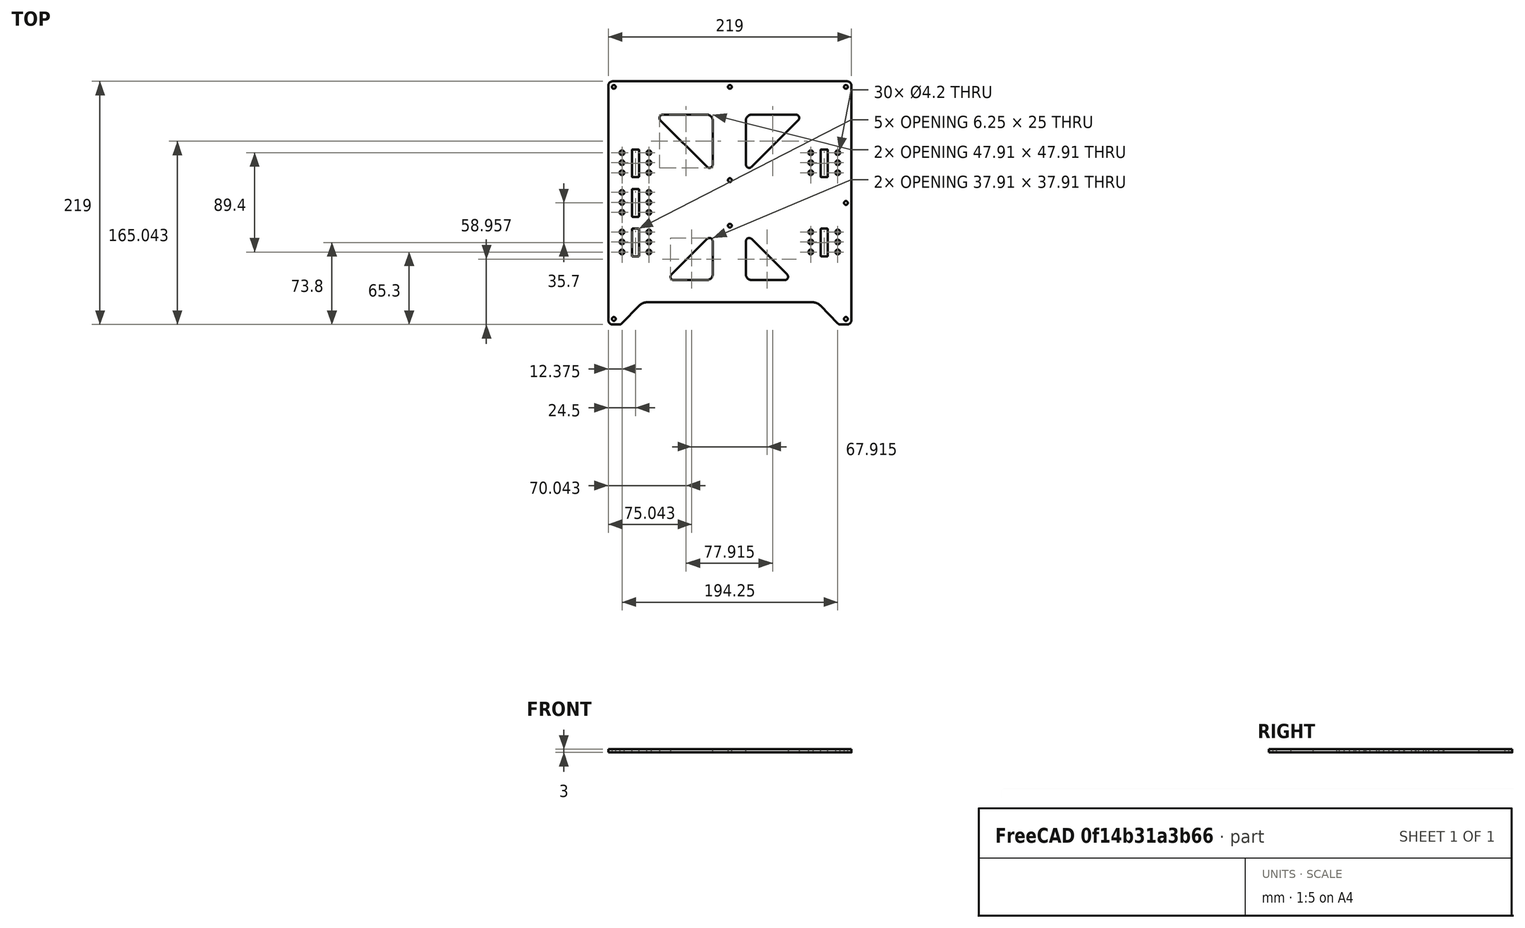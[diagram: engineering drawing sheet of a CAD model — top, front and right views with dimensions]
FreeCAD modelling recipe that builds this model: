
FCSTD DOCUMENT  (FreeCAD 0.18R)
Label: carriage-plate
License: All rights reserved
LicenseURL: http://en.wikipedia.org/wiki/All_rights_reserved
objects: Sketcher::SketchObject×1, PartDesign::Pad×1, PartDesign::Body×1
note: 4 computed .brp shape members not serialized (recipe doc carries the construction recipe); baked Part::Feature solids carry a one-line shape summary decoded from their .brp

FEATURE [Sketcher::SketchObject] Sketch009  label="Plate Sketch"
  MapMode = 5
  Support = -> [XY_Plane]
  sketch-geometry (118):
    g0: LineSegment StartX=-215 StartY=219 StartZ=0 EndX=-4 EndY=219 EndZ=0
    g1: LineSegment StartX=0 StartY=215 StartZ=0 EndX=0 EndY=4 EndZ=0
    g2: ArcOfCircle CenterX=-4 CenterY=215 CenterZ=0 NormalX=0 NormalY=0 NormalZ=1 AngleXU=0 Radius=4 StartAngle=-3.6e-15 EndAngle=1.5708
    g3: LineSegment StartX=-219 StartY=215 StartZ=0 EndX=-219 EndY=4 EndZ=0
    g4: ArcOfCircle CenterX=-215 CenterY=215 CenterZ=0 NormalX=0 NormalY=0 NormalZ=1 AngleXU=0 Radius=4 StartAngle=1.5708 EndAngle=3.14159
    g5: LineSegment StartX=-10 StartY=0 StartZ=0 EndX=-4 EndY=0 EndZ=0
    g6: ArcOfCircle CenterX=-4 CenterY=4 CenterZ=0 NormalX=0 NormalY=0 NormalZ=1 AngleXU=0 Radius=4 StartAngle=4.71239 EndAngle=6.28319
    g7: LineSegment StartX=-215 StartY=1.3e-15 StartZ=0 EndX=-209 EndY=1.3e-15 EndZ=0
    g8: ArcOfCircle CenterX=-215 CenterY=4 CenterZ=0 NormalX=0 NormalY=0 NormalZ=1 AngleXU=0 Radius=4 StartAngle=3.14159 EndAngle=4.71239
    g9: LineSegment StartX=-184 StartY=20 StartZ=0 EndX=-35 EndY=20 EndZ=0
    g10: LineSegment StartX=-27.817 StartY=16.9574 StartZ=0 EndX=-12.3608 EndY=1 EndZ=0
    g11: ArcOfCircle CenterX=-10 CenterY=3.28664 CenterZ=0 NormalX=0 NormalY=0 NormalZ=1 AngleXU=0 Radius=3.28664 StartAngle=3.91104 EndAngle=4.71239
    g12: ArcOfCircle CenterX=-35 CenterY=10 CenterZ=0 NormalX=0 NormalY=0 NormalZ=1 AngleXU=0 Radius=10 StartAngle=0.769447 EndAngle=1.5708
    g13: LineSegment StartX=-206.639 StartY=1 StartZ=0 EndX=-191.183 EndY=16.9574 EndZ=0
    g14: ArcOfCircle CenterX=-184 CenterY=10 CenterZ=0 NormalX=0 NormalY=0 NormalZ=1 AngleXU=0 Radius=10 StartAngle=1.5708 EndAngle=2.37215
    g15: ArcOfCircle CenterX=-209 CenterY=3.28664 CenterZ=0 NormalX=0 NormalY=0 NormalZ=1 AngleXU=0 Radius=3.28664 StartAngle=4.71239 EndAngle=5.51374
    g16: Circle CenterX=-5 CenterY=214 CenterZ=0 NormalX=0 NormalY=0 NormalZ=1 AngleXU=0 Radius=1.7
    g17: Circle CenterX=-5 CenterY=109.5 CenterZ=0 NormalX=0 NormalY=0 NormalZ=1 AngleXU=0 Radius=1.7
    g18: Circle CenterX=-5 CenterY=5 CenterZ=0 NormalX=0 NormalY=0 NormalZ=1 AngleXU=0 Radius=1.7
    g19: Circle CenterX=-109.5 CenterY=214 CenterZ=0 NormalX=0 NormalY=0 NormalZ=1 AngleXU=0 Radius=1.7
    g20: Circle CenterX=-214 CenterY=214 CenterZ=0 NormalX=0 NormalY=0 NormalZ=1 AngleXU=0 Radius=1.7
    g21: Circle CenterX=-214 CenterY=5 CenterZ=0 NormalX=0 NormalY=0 NormalZ=1 AngleXU=0 Radius=1.7
    g22: Circle CenterX=-109.5 CenterY=130 CenterZ=0 NormalX=0 NormalY=0 NormalZ=1 AngleXU=0 Radius=1.7
    g23: Circle CenterX=-109.5 CenterY=89 CenterZ=0 NormalX=0 NormalY=0 NormalZ=1 AngleXU=0 Radius=1.7
    g24: LineSegment StartX=-27.625 StartY=85.8 StartZ=0 EndX=-27.625 EndY=61.8 EndZ=0
    g25: LineSegment StartX=-21.375 StartY=85.8 StartZ=0 EndX=-21.375 EndY=61.8 EndZ=0
    g26: LineSegment StartX=-27.125 StartY=61.3 StartZ=0 EndX=-21.875 EndY=61.3 EndZ=0
    g27: LineSegment StartX=-27.125 StartY=86.3 StartZ=0 EndX=-21.875 EndY=86.3 EndZ=0
    g28: ArcOfCircle CenterX=-27.125 CenterY=85.8 CenterZ=0 NormalX=0 NormalY=0 NormalZ=1 AngleXU=0 Radius=0.5 StartAngle=1.5708 EndAngle=3.14159
    g29: ArcOfCircle CenterX=-27.125 CenterY=61.8 CenterZ=0 NormalX=0 NormalY=0 NormalZ=1 AngleXU=0 Radius=0.5 StartAngle=3.14159 EndAngle=4.71239
    g30: ArcOfCircle CenterX=-21.875 CenterY=85.8 CenterZ=0 NormalX=0 NormalY=0 NormalZ=1 AngleXU=0 Radius=0.5 StartAngle=1.5e-15 EndAngle=1.5708
    g31: ArcOfCircle CenterX=-21.875 CenterY=61.8 CenterZ=0 NormalX=0 NormalY=0 NormalZ=1 AngleXU=0 Radius=0.5 StartAngle=4.71239 EndAngle=6.28319
    g32: Circle CenterX=-12.375 CenterY=83.3 CenterZ=0 NormalX=0 NormalY=0 NormalZ=1 AngleXU=0 Radius=2.1
    g33: Circle CenterX=-36.625 CenterY=83.3 CenterZ=0 NormalX=0 NormalY=0 NormalZ=1 AngleXU=0 Radius=2.1
    g34: Circle CenterX=-12.375 CenterY=74.3 CenterZ=0 NormalX=0 NormalY=0 NormalZ=1 AngleXU=0 Radius=2.1
    g35: Circle CenterX=-12.375 CenterY=65.3 CenterZ=0 NormalX=0 NormalY=0 NormalZ=1 AngleXU=0 Radius=2.1
    g36: Circle CenterX=-36.625 CenterY=74.3 CenterZ=0 NormalX=0 NormalY=0 NormalZ=1 AngleXU=0 Radius=2.1
    g37: Circle CenterX=-36.625 CenterY=65.3 CenterZ=0 NormalX=0 NormalY=0 NormalZ=1 AngleXU=0 Radius=2.1
    g38: LineSegment StartX=-90 StartY=189 StartZ=0 EndX=-50 EndY=189 EndZ=0
    g39: LineSegment StartX=-95 StartY=184 StartZ=0 EndX=-95 EndY=144 EndZ=0
    g40: LineSegment StartX=-90 StartY=141.929 StartZ=0 EndX=-47.9289 EndY=184 EndZ=0
    g41: ArcOfCircle CenterX=-90 CenterY=184 CenterZ=0 NormalX=0 NormalY=0 NormalZ=1 AngleXU=0 Radius=5 StartAngle=1.5708 EndAngle=3.14159
    g42: ArcOfCircle CenterX=-92.0711 CenterY=144 CenterZ=0 NormalX=0 NormalY=0 NormalZ=1 AngleXU=0 Radius=2.92893 StartAngle=3.14159 EndAngle=5.49779
    g43: ArcOfCircle CenterX=-50 CenterY=186.071 CenterZ=0 NormalX=0 NormalY=0 NormalZ=1 AngleXU=0 Radius=2.92893 StartAngle=5.49779 EndAngle=7.85398
    g44: LineSegment StartX=-170 StartY=189 StartZ=0 EndX=-130 EndY=189 EndZ=0
    g45: LineSegment StartX=-125 StartY=184 StartZ=0 EndX=-125 EndY=144 EndZ=0
    g46: LineSegment StartX=-172.071 StartY=184 StartZ=0 EndX=-130 EndY=141.929 EndZ=0
    g47: ArcOfCircle CenterX=-130 CenterY=184 CenterZ=0 NormalX=0 NormalY=0 NormalZ=1 AngleXU=0 Radius=5 StartAngle=0 EndAngle=1.5708
    g48: ArcOfCircle CenterX=-170 CenterY=186.071 CenterZ=0 NormalX=0 NormalY=0 NormalZ=1 AngleXU=0 Radius=2.92893 StartAngle=1.5708 EndAngle=3.92699
    g49: ArcOfCircle CenterX=-127.929 CenterY=144 CenterZ=0 NormalX=0 NormalY=0 NormalZ=1 AngleXU=0 Radius=2.92893 StartAngle=3.92699 EndAngle=6.28319
    g50: LineSegment StartX=-95 StartY=75 StartZ=0 EndX=-95 EndY=45 EndZ=0
    g51: LineSegment StartX=-90 StartY=77.0711 StartZ=0 EndX=-57.9289 EndY=45 EndZ=0
    g52: LineSegment StartX=-90 StartY=40 StartZ=0 EndX=-60 EndY=40 EndZ=0
    g53: ArcOfCircle CenterX=-92.0711 CenterY=75 CenterZ=0 NormalX=0 NormalY=0 NormalZ=1 AngleXU=0 Radius=2.92893 StartAngle=0.785398 EndAngle=3.14159
    g54: ArcOfCircle CenterX=-90 CenterY=45 CenterZ=0 NormalX=0 NormalY=0 NormalZ=1 AngleXU=0 Radius=5 StartAngle=3.14159 EndAngle=4.71239
    g55: ArcOfCircle CenterX=-60 CenterY=42.9289 CenterZ=0 NormalX=0 NormalY=0 NormalZ=1 AngleXU=0 Radius=2.92893 StartAngle=4.71239 EndAngle=7.06858
    g56: LineSegment StartX=-162.071 StartY=45 StartZ=0 EndX=-130 EndY=77.0711 EndZ=0
    g57: LineSegment StartX=-125 StartY=75 StartZ=0 EndX=-125 EndY=45 EndZ=0
    g58: LineSegment StartX=-160 StartY=40 StartZ=0 EndX=-130 EndY=40 EndZ=0
    g59: ArcOfCircle CenterX=-127.929 CenterY=75 CenterZ=0 NormalX=0 NormalY=0 NormalZ=1 AngleXU=0 Radius=2.92893 StartAngle=1.7e-15 EndAngle=2.35619
    g60: ArcOfCircle CenterX=-130 CenterY=45 CenterZ=0 NormalX=0 NormalY=0 NormalZ=1 AngleXU=0 Radius=5 StartAngle=4.71239 EndAngle=6.28319
    g61: ArcOfCircle CenterX=-160 CenterY=42.9289 CenterZ=0 NormalX=0 NormalY=0 NormalZ=1 AngleXU=0 Radius=2.92893 StartAngle=2.35619 EndAngle=4.71239
    g62: LineSegment StartX=-27.625 StartY=157.2 StartZ=0 EndX=-27.625 EndY=133.2 EndZ=0
    g63: LineSegment StartX=-21.375 StartY=157.2 StartZ=0 EndX=-21.375 EndY=133.2 EndZ=0
    g64: LineSegment StartX=-27.125 StartY=132.7 StartZ=0 EndX=-21.875 EndY=132.7 EndZ=0
    g65: LineSegment StartX=-27.125 StartY=157.7 StartZ=0 EndX=-21.875 EndY=157.7 EndZ=0
    g66: ArcOfCircle CenterX=-27.125 CenterY=157.2 CenterZ=0 NormalX=0 NormalY=0 NormalZ=1 AngleXU=0 Radius=0.5 StartAngle=1.5708 EndAngle=3.14159
    g67: ArcOfCircle CenterX=-27.125 CenterY=133.2 CenterZ=0 NormalX=0 NormalY=0 NormalZ=1 AngleXU=0 Radius=0.5 StartAngle=3.14159 EndAngle=4.71239
    g68: ArcOfCircle CenterX=-21.875 CenterY=157.2 CenterZ=0 NormalX=0 NormalY=0 NormalZ=1 AngleXU=0 Radius=0.5 StartAngle=-1.91456e-11 EndAngle=1.5708
    g69: ArcOfCircle CenterX=-21.875 CenterY=133.2 CenterZ=0 NormalX=0 NormalY=0 NormalZ=1 AngleXU=0 Radius=0.5 StartAngle=4.71239 EndAngle=6.28319
    g70: Circle CenterX=-12.375 CenterY=154.7 CenterZ=0 NormalX=0 NormalY=0 NormalZ=1 AngleXU=0 Radius=2.1
    g71: Circle CenterX=-36.625 CenterY=154.7 CenterZ=0 NormalX=0 NormalY=0 NormalZ=1 AngleXU=0 Radius=2.1
    g72: Circle CenterX=-12.375 CenterY=145.7 CenterZ=0 NormalX=0 NormalY=0 NormalZ=1 AngleXU=0 Radius=2.1
    g73: Circle CenterX=-12.375 CenterY=136.7 CenterZ=0 NormalX=0 NormalY=0 NormalZ=1 AngleXU=0 Radius=2.1
    g74: Circle CenterX=-36.625 CenterY=145.7 CenterZ=0 NormalX=0 NormalY=0 NormalZ=1 AngleXU=0 Radius=2.1
    g75: Circle CenterX=-36.625 CenterY=136.7 CenterZ=0 NormalX=0 NormalY=0 NormalZ=1 AngleXU=0 Radius=2.1
    g76: LineSegment StartX=-197.625 StartY=85.8 StartZ=0 EndX=-197.625 EndY=61.8 EndZ=0
    g77: LineSegment StartX=-191.375 StartY=85.8 StartZ=0 EndX=-191.375 EndY=61.8 EndZ=0
    g78: LineSegment StartX=-197.125 StartY=61.3 StartZ=0 EndX=-191.875 EndY=61.3 EndZ=0
    g79: LineSegment StartX=-197.125 StartY=86.3 StartZ=0 EndX=-191.875 EndY=86.3 EndZ=0
    g80: ArcOfCircle CenterX=-197.125 CenterY=85.8 CenterZ=0 NormalX=0 NormalY=0 NormalZ=1 AngleXU=0 Radius=0.5 StartAngle=1.5708 EndAngle=3.14159
    g81: ArcOfCircle CenterX=-197.125 CenterY=61.8 CenterZ=0 NormalX=0 NormalY=0 NormalZ=1 AngleXU=0 Radius=0.5 StartAngle=3.14159 EndAngle=4.71239
    g82: ArcOfCircle CenterX=-191.875 CenterY=85.8 CenterZ=0 NormalX=0 NormalY=0 NormalZ=1 AngleXU=0 Radius=0.5 StartAngle=-1.91545e-11 EndAngle=1.5708
    g83: ArcOfCircle CenterX=-191.875 CenterY=61.8 CenterZ=0 NormalX=0 NormalY=0 NormalZ=1 AngleXU=0 Radius=0.5 StartAngle=4.71239 EndAngle=6.28319
    g84: Circle CenterX=-182.375 CenterY=83.3 CenterZ=0 NormalX=0 NormalY=0 NormalZ=1 AngleXU=0 Radius=2.1
    g85: Circle CenterX=-206.625 CenterY=83.3 CenterZ=0 NormalX=0 NormalY=0 NormalZ=1 AngleXU=0 Radius=2.1
    g86: Circle CenterX=-182.375 CenterY=74.3 CenterZ=0 NormalX=0 NormalY=0 NormalZ=1 AngleXU=0 Radius=2.1
    g87: Circle CenterX=-182.375 CenterY=65.3 CenterZ=0 NormalX=0 NormalY=0 NormalZ=1 AngleXU=0 Radius=2.1
    g88: Circle CenterX=-206.625 CenterY=74.3 CenterZ=0 NormalX=0 NormalY=0 NormalZ=1 AngleXU=0 Radius=2.1
    g89: Circle CenterX=-206.625 CenterY=65.3 CenterZ=0 NormalX=0 NormalY=0 NormalZ=1 AngleXU=0 Radius=2.1
    g90: LineSegment StartX=-197.625 StartY=157.2 StartZ=0 EndX=-197.625 EndY=133.2 EndZ=0
    g91: LineSegment StartX=-191.375 StartY=157.2 StartZ=0 EndX=-191.375 EndY=133.2 EndZ=0
    g92: LineSegment StartX=-197.125 StartY=132.7 StartZ=0 EndX=-191.875 EndY=132.7 EndZ=0
    g93: LineSegment StartX=-197.125 StartY=157.7 StartZ=0 EndX=-191.875 EndY=157.7 EndZ=0
    g94: ArcOfCircle CenterX=-197.125 CenterY=157.2 CenterZ=0 NormalX=0 NormalY=0 NormalZ=1 AngleXU=0 Radius=0.5 StartAngle=1.5708 EndAngle=3.14159
    g95: ArcOfCircle CenterX=-197.125 CenterY=133.2 CenterZ=0 NormalX=0 NormalY=0 NormalZ=1 AngleXU=0 Radius=0.5 StartAngle=3.14159 EndAngle=4.71239
    g96: ArcOfCircle CenterX=-191.875 CenterY=157.2 CenterZ=0 NormalX=0 NormalY=0 NormalZ=1 AngleXU=0 Radius=0.5 StartAngle=-1.91234e-11 EndAngle=1.5708
    g97: ArcOfCircle CenterX=-191.875 CenterY=133.2 CenterZ=0 NormalX=0 NormalY=0 NormalZ=1 AngleXU=0 Radius=0.5 StartAngle=4.71239 EndAngle=6.28319
    g98: Circle CenterX=-182.375 CenterY=154.7 CenterZ=0 NormalX=0 NormalY=0 NormalZ=1 AngleXU=0 Radius=2.1
    g99: Circle CenterX=-206.625 CenterY=154.7 CenterZ=0 NormalX=0 NormalY=0 NormalZ=1 AngleXU=0 Radius=2.1
    g100: Circle CenterX=-182.375 CenterY=145.7 CenterZ=0 NormalX=0 NormalY=0 NormalZ=1 AngleXU=0 Radius=2.1
    g101: Circle CenterX=-182.375 CenterY=136.7 CenterZ=0 NormalX=0 NormalY=0 NormalZ=1 AngleXU=0 Radius=2.1
    g102: Circle CenterX=-206.625 CenterY=145.7 CenterZ=0 NormalX=0 NormalY=0 NormalZ=1 AngleXU=0 Radius=2.1
    g103: Circle CenterX=-206.625 CenterY=136.7 CenterZ=0 NormalX=0 NormalY=0 NormalZ=1 AngleXU=0 Radius=2.1
    g104: LineSegment StartX=-197.625 StartY=121.5 StartZ=0 EndX=-197.625 EndY=97.5 EndZ=0
    g105: LineSegment StartX=-191.375 StartY=121.5 StartZ=0 EndX=-191.375 EndY=97.5 EndZ=0
    g106: LineSegment StartX=-197.125 StartY=97 StartZ=0 EndX=-191.875 EndY=97 EndZ=0
    g107: LineSegment StartX=-197.125 StartY=122 StartZ=0 EndX=-191.875 EndY=122 EndZ=0
    g108: ArcOfCircle CenterX=-197.125 CenterY=121.5 CenterZ=0 NormalX=0 NormalY=0 NormalZ=1 AngleXU=0 Radius=0.5 StartAngle=1.5708 EndAngle=3.14159
    g109: ArcOfCircle CenterX=-197.125 CenterY=97.5 CenterZ=0 NormalX=0 NormalY=0 NormalZ=1 AngleXU=0 Radius=0.5 StartAngle=3.14159 EndAngle=4.71239
    g110: ArcOfCircle CenterX=-191.875 CenterY=121.5 CenterZ=0 NormalX=0 NormalY=0 NormalZ=1 AngleXU=0 Radius=0.5 StartAngle=-1.91429e-11 EndAngle=1.5708
    g111: ArcOfCircle CenterX=-191.875 CenterY=97.5 CenterZ=0 NormalX=0 NormalY=0 NormalZ=1 AngleXU=0 Radius=0.5 StartAngle=4.71239 EndAngle=6.28319
    g112: Circle CenterX=-182.375 CenterY=119 CenterZ=0 NormalX=0 NormalY=0 NormalZ=1 AngleXU=0 Radius=2.1
    g113: Circle CenterX=-206.625 CenterY=119 CenterZ=0 NormalX=0 NormalY=0 NormalZ=1 AngleXU=0 Radius=2.1
    g114: Circle CenterX=-182.375 CenterY=110 CenterZ=0 NormalX=0 NormalY=0 NormalZ=1 AngleXU=0 Radius=2.1
    g115: Circle CenterX=-182.375 CenterY=101 CenterZ=0 NormalX=0 NormalY=0 NormalZ=1 AngleXU=0 Radius=2.1
    g116: Circle CenterX=-206.625 CenterY=110 CenterZ=0 NormalX=0 NormalY=0 NormalZ=1 AngleXU=0 Radius=2.1
    g117: Circle CenterX=-206.625 CenterY=101 CenterZ=0 NormalX=0 NormalY=0 NormalZ=1 AngleXU=0 Radius=2.1
  constraints (314):
    c: Vertical(g1)
    c: Tangent(g0,g2) = 1.5708
    c: Tangent(g1,g2) = 1.5708
    c: Equal(g0,g1)
    c: DistanceX(g0,g1) = 4
    c: Horizontal(g0)
    c: Equal(g1,g3)
    c: Vertical(g3)
    c: Tangent(g0,g4) = 1.5708
    c: Tangent(g3,g4) = -1.5708
    c: DistanceX(g3,g0) = 4
    c: Horizontal(g5)
    c: Tangent(g1,g6) = 1.5708
    c: Tangent(g5,g6) = -1.5708
    c: DistanceX(g5,g1) = 4
    c: DistanceY(g-1,g5) = 0
    c: Tangent(g3,g8) = -1.5708
    c: Tangent(g7,g8) = -1.5708
    c: DistanceX(g3,g7) = 4
    c: Horizontal(g7)
    c: DistanceX(g1,g-1) = 0
    c: Horizontal(g9)
    c: Tangent(g10,g11) = -1.5708
    c: Tangent(g5,g11) = -1.5708
    c: Tangent(g9,g12) = 1.5708
    c: Tangent(g10,g12) = 1.5708
    c: DistanceY(g-1,g9) = 20
    c: DistanceX(g9,g1) = 35
    c: Tangent(g9,g14) = 1.5708
    c: Tangent(g13,g14) = 1.5708
    c: DistanceX(g3,g9) = 35
    c: Tangent(g13,g15) = -1.5708
    c: Tangent(g7,g15) = -1.5708
    c: DistanceY(g7,g13) = 1
    c: DistanceX(g5,g-1) = 10
    c: DistanceX(g3,g7) = 10
    c: DistanceY(g-1,g10) = 1
    c: DistanceY(g-1,g12) = 10
    c: DistanceY(g7,g14) = 10
    c: DistanceX(g9,g9) = 149
    c: Diameter(g16) = 3.4
    c: DistanceX(g16,g-1) = 5
    c: DistanceY(g-1,g16) = 214
    c: Equal(g17,g16)
    c: DistanceX(g17,g16) = 0
    c: DistanceY(g-1,g17) = 109.5
    c: Equal(g16,g18)
    c: DistanceX(g18,g17) = 0
    c: DistanceY(g-1,g18) = 5
    c: Equal(g16,g19)
    c: DistanceY(g19,g16) = 0
    c: DistanceX(g19,g-1) = 109.5
    c: Equal(g20,g19)
    c: DistanceY(g20,g19) = 0
    c: DistanceX(g20,g-1) = 214
    c: Equal(g16,g21)
    c: DistanceX(g20,g21) = 0
    c: DistanceY(g18,g21) = 0
    c: Equal(g22,g16)
    c: Equal(g23,g16)
    c: DistanceX(g19,g22) = 0
    c: DistanceX(g22,g23) = 0
    c: DistanceY(g-1,g23) = 89
    c: DistanceY(g23,g22) = 41
    c: Vertical(g24)
    c: Vertical(g25)
    c: Horizontal(g26)
    c: Horizontal(g27)
    c: Equal(g24,g25)
    c: Equal(g27,g26)
    c: Tangent(g27,g28) = 1.5708
    c: Tangent(g24,g28) = -1.5708
    c: Tangent(g24,g29) = -1.5708
    c: Tangent(g26,g29) = -1.5708
    c: Tangent(g27,g30) = 1.5708
    c: Tangent(g25,g30) = 1.5708
    c: Tangent(g26,g31) = -1.5708
    c: Tangent(g25,g31) = 1.5708
    c: DistanceY(g25,g24) = 0
    c: DistanceX(g24,g25) = 6.25
    c: DistanceX(g24,g27) = 0.5
    c: DistanceY(g26,g27) = 25
    c: DistanceX(g25,g-1) = 21.375
    c: DistanceY(g26,g-1) = -61.3
    c: Diameter(g32) = 4.2
    c: DistanceY(g32,g27) = 3
    c: DistanceX(g25,g32) = 9
    c: DistanceY(g32,g33) = 0
    c: DistanceX(g33,g24) = 9
    c: DistanceX(g34,g32) = 0
    c: DistanceY(g34,g32) = 9
    c: DistanceX(g35,g34) = 0
    c: DistanceY(g35,g34) = 9
    c: Equal(g35,g37)
    c: Equal(g37,g36)
    c: Equal(g36,g34)
    c: Equal(g34,g33)
    c: Equal(g33,g32)
    c: DistanceY(g34,g36) = 0
    c: DistanceY(g35,g37) = 0
    c: DistanceX(g36,g33) = 0
    c: DistanceX(g37,g36) = 0
    c: Horizontal(g38)
    c: Vertical(g39)
    c: Tangent(g38,g41) = 1.5708
    c: Tangent(g39,g41) = -1.5708
    c: Tangent(g39,g42) = -1.5708
    c: Tangent(g40,g42) = -1.5708
    c: Tangent(g38,g43) = 1.5708
    c: Tangent(g40,g43) = -1.5708
    c: DistanceY(g39,g39) = 40
    c: DistanceX(g38,g38) = 40
    c: DistanceX(g39,g38) = 5
    c: DistanceX(g39,g40) = 5
    c: DistanceY(g40,g38) = 5
    c: DistanceX(g39,g-1) = 95
    c: DistanceY(g-1,g38) = 189
    c: Horizontal(g44)
    c: Vertical(g45)
    c: Tangent(g44,g47) = 1.5708
    c: Tangent(g45,g47) = 1.5708
    c: Tangent(g44,g48) = 1.5708
    c: Tangent(g46,g48) = -1.5708
    c: Tangent(g46,g49) = -1.5708
    c: Tangent(g45,g49) = 1.5708
    c: DistanceX(g44,g44) = 40
    c: DistanceY(g45,g45) = 40
    c: DistanceX(g46,g45) = 5
    c: DistanceX(g44,g45) = 5
    c: DistanceY(g46,g44) = 5
    c: DistanceX(g45,g39) = 30
    c: DistanceY(g39,g45) = 0
    c: Vertical(g50)
    c: Horizontal(g52)
    c: Tangent(g50,g53) = -1.5708
    c: Tangent(g51,g53) = 1.5708
    c: Tangent(g50,g54) = -1.5708
    c: Tangent(g52,g54) = -1.5708
    c: Tangent(g51,g55) = 1.5708
    c: Tangent(g52,g55) = -1.5708
    c: DistanceX(g50,g39) = 0
    c: DistanceY(g50,g50) = 30
    c: DistanceX(g52,g52) = 30
    c: DistanceY(g52,g51) = 5
    c: DistanceX(g50,g51) = 5
    c: DistanceX(g50,g52) = 5
    c: DistanceY(g-1,g52) = 40
    c: Tangent(g56,g59) = 1.5708
    c: Tangent(g57,g59) = 1.5708
    c: Tangent(g57,g60) = 1.5708
    c: Tangent(g58,g60) = -1.5708
    c: Tangent(g58,g61) = -1.5708
    c: Tangent(g56,g61) = 1.5708
    c: DistanceY(g57,g57) = 30
    c: DistanceX(g57,g45) = 0
    c: Vertical(g57)
    c: Horizontal(g58)
    c: DistanceX(g58,g58) = 30
    c: DistanceY(g58,g52) = 0
    c: DistanceY(g58,g56) = 5
    c: DistanceY(g58,g57) = 5
    c: DistanceX(g56,g57) = 5
    c: Vertical(g62)
    c: Vertical(g63)
    c: Horizontal(g64)
    c: Horizontal(g65)
    c: Equal(g62,g63)
    c: Equal(g65,g64)
    c: Tangent(g65,g66) = 1.5708
    c: Tangent(g62,g66) = -1.5708
    c: Tangent(g62,g67) = -1.5708
    c: Tangent(g64,g67) = -1.5708
    c: Tangent(g65,g68) = 1.5708
    c: Tangent(g63,g68) = 1.5708
    c: Tangent(g64,g69) = -1.5708
    c: Tangent(g63,g69) = 1.5708
    c: DistanceY(g63,g62) = 0
    c: DistanceX(g62,g63) = 6.25
    c: DistanceX(g62,g65) = 0.5
    c: DistanceY(g64,g65) = 25
    c: DistanceX(g63,g-1) = 21.375
    c: DistanceY(g64,g-1) = -132.7
    c: Diameter(g70) = 4.2
    c: DistanceY(g70,g65) = 3
    c: DistanceX(g63,g70) = 9
    c: DistanceY(g70,g71) = 0
    c: DistanceX(g71,g62) = 9
    c: DistanceX(g72,g70) = 0
    c: DistanceY(g72,g70) = 9
    c: DistanceX(g73,g72) = 0
    c: DistanceY(g73,g72) = 9
    c: Equal(g73,g75)
    c: Equal(g75,g74)
    c: Equal(g74,g72)
    c: Equal(g72,g71)
    c: Equal(g71,g70)
    c: DistanceY(g72,g74) = 0
    c: DistanceY(g73,g75) = 0
    c: DistanceX(g74,g71) = 0
    c: DistanceX(g75,g74) = 0
    c: Vertical(g76)
    c: Vertical(g77)
    c: Horizontal(g78)
    c: Horizontal(g79)
    c: Equal(g76,g77)
    c: Equal(g79,g78)
    c: Tangent(g79,g80) = 1.5708
    c: Tangent(g76,g80) = -1.5708
    c: Tangent(g76,g81) = -1.5708
    c: Tangent(g78,g81) = -1.5708
    c: Tangent(g79,g82) = 1.5708
    c: Tangent(g77,g82) = 1.5708
    c: Tangent(g78,g83) = -1.5708
    c: Tangent(g77,g83) = 1.5708
    c: DistanceY(g77,g76) = 0
    c: DistanceX(g76,g77) = 6.25
    c: DistanceX(g76,g79) = 0.5
    c: DistanceY(g78,g79) = 25
    c: DistanceX(g77,g-1) = 191.375
    c: DistanceY(g78,g-1) = -61.3
    c: Diameter(g84) = 4.2
    c: DistanceY(g84,g79) = 3
    c: DistanceX(g77,g84) = 9
    c: DistanceY(g84,g85) = 0
    c: DistanceX(g85,g76) = 9
    c: DistanceX(g86,g84) = 0
    c: DistanceY(g86,g84) = 9
    c: DistanceX(g87,g86) = 0
    c: DistanceY(g87,g86) = 9
    c: Equal(g87,g89)
    c: Equal(g89,g88)
    c: Equal(g88,g86)
    c: Equal(g86,g85)
    c: Equal(g85,g84)
    c: DistanceY(g86,g88) = 0
    c: DistanceY(g87,g89) = 0
    c: DistanceX(g88,g85) = 0
    c: DistanceX(g89,g88) = 0
    c: Vertical(g90)
    c: Vertical(g91)
    c: Horizontal(g92)
    c: Horizontal(g93)
    c: Equal(g90,g91)
    c: Equal(g93,g92)
    c: Tangent(g93,g94) = 1.5708
    c: Tangent(g90,g94) = -1.5708
    c: Tangent(g90,g95) = -1.5708
    c: Tangent(g92,g95) = -1.5708
    c: Tangent(g93,g96) = 1.5708
    c: Tangent(g91,g96) = 1.5708
    c: Tangent(g92,g97) = -1.5708
    c: Tangent(g91,g97) = 1.5708
    c: DistanceY(g91,g90) = 0
    c: DistanceX(g90,g91) = 6.25
    c: DistanceX(g90,g93) = 0.5
    c: DistanceY(g92,g93) = 25
    c: DistanceX(g91,g-1) = 191.375
    c: DistanceY(g92,g-1) = -132.7
    c: Diameter(g98) = 4.2
    c: DistanceY(g98,g93) = 3
    c: DistanceX(g91,g98) = 9
    c: DistanceY(g98,g99) = 0
    c: DistanceX(g99,g90) = 9
    c: DistanceX(g100,g98) = 0
    c: DistanceY(g100,g98) = 9
    c: DistanceX(g101,g100) = 0
    c: DistanceY(g101,g100) = 9
    c: Equal(g101,g103)
    c: Equal(g103,g102)
    c: Equal(g102,g100)
    c: Equal(g100,g99)
    c: Equal(g99,g98)
    c: DistanceY(g100,g102) = 0
    c: DistanceY(g101,g103) = 0
    c: DistanceX(g102,g99) = 0
    c: DistanceX(g103,g102) = 0
    c: Vertical(g104)
    c: Vertical(g105)
    c: Horizontal(g106)
    c: Horizontal(g107)
    c: Equal(g104,g105)
    c: Equal(g107,g106)
    c: Tangent(g107,g108) = 1.5708
    c: Tangent(g104,g108) = -1.5708
    c: Tangent(g104,g109) = -1.5708
    c: Tangent(g106,g109) = -1.5708
    c: Tangent(g107,g110) = 1.5708
    c: Tangent(g105,g110) = 1.5708
    c: Tangent(g106,g111) = -1.5708
    c: Tangent(g105,g111) = 1.5708
    c: DistanceY(g105,g104) = 0
    c: DistanceX(g104,g105) = 6.25
    c: DistanceX(g104,g107) = 0.5
    c: DistanceY(g106,g107) = 25
    c: DistanceX(g105,g-1) = 191.375
    c: DistanceY(g106,g-1) = -97
    c: Diameter(g112) = 4.2
    c: DistanceY(g112,g107) = 3
    c: DistanceX(g105,g112) = 9
    c: DistanceY(g112,g113) = 0
    c: DistanceX(g113,g104) = 9
    c: DistanceX(g114,g112) = 0
    c: DistanceY(g114,g112) = 9
    c: DistanceX(g115,g114) = 0
    c: DistanceY(g115,g114) = 9
    c: Equal(g115,g117)
    c: Equal(g117,g116)
    c: Equal(g116,g114)
    c: Equal(g114,g113)
    c: Equal(g113,g112)
    c: DistanceY(g114,g116) = 0
    c: DistanceY(g115,g117) = 0
    c: DistanceX(g116,g113) = 0
    c: DistanceX(g117,g116) = 0
FEATURE [PartDesign::Pad] Pad
  Length = 3
  Length2 = 100
  Profile = -> Sketch009
  Type = 0
FEATURE [PartDesign::Body] Body  label="carriage-plate"
  Group = -> [Sketch009,Pad]
  Origin = -> Origin
  Tip = -> Pad
